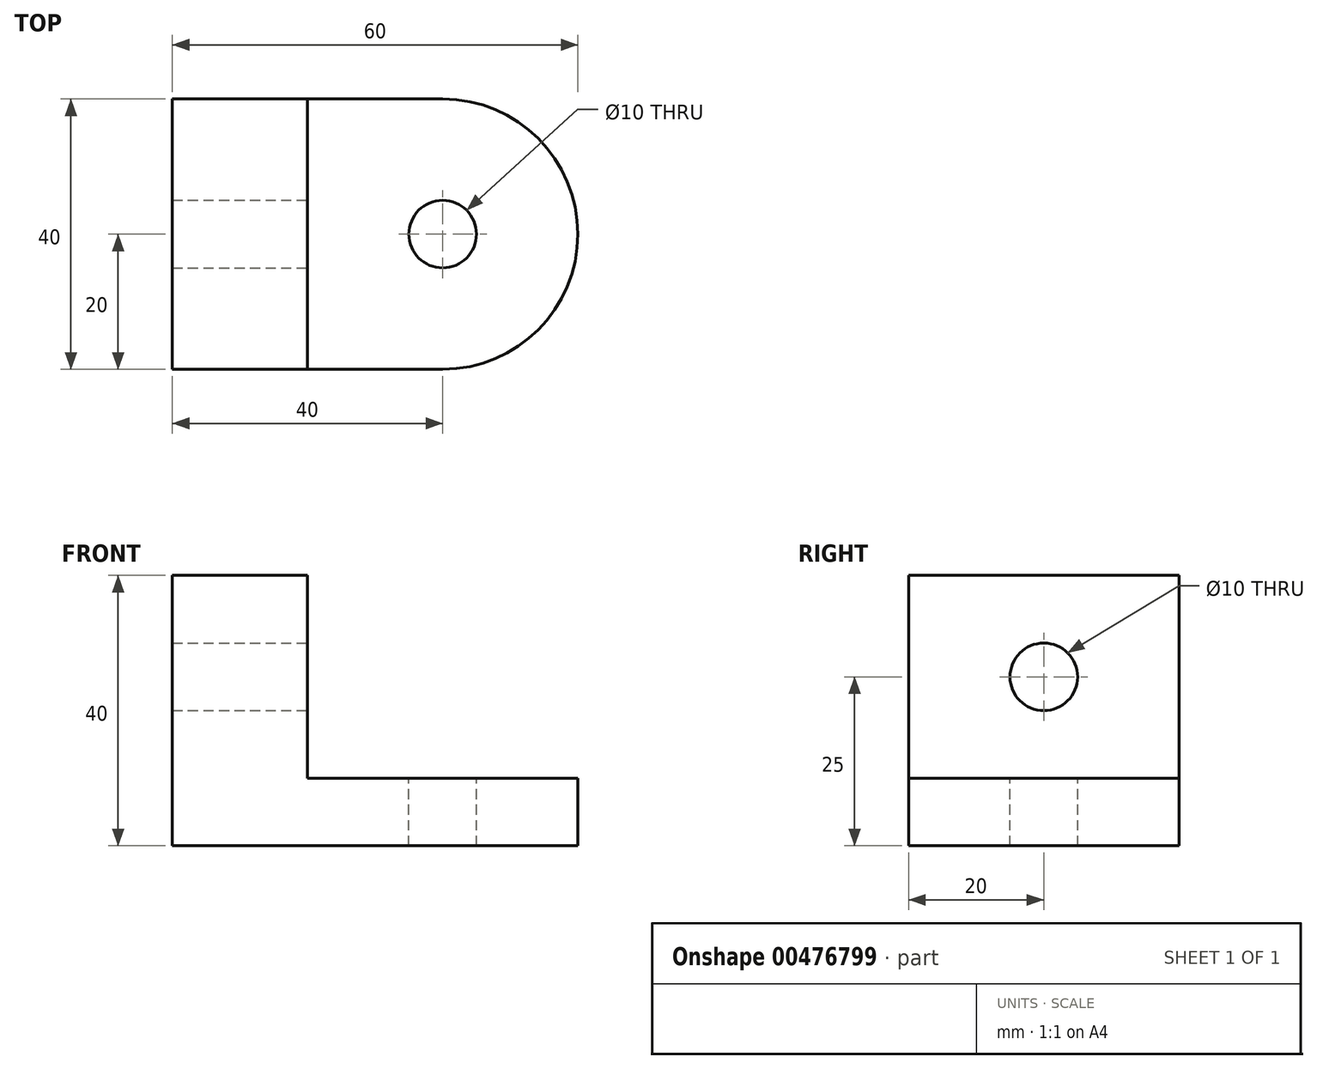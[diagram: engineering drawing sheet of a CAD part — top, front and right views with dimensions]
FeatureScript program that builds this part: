
annotation { "Feature Type Name" : "Feature", "Feature Type Description" : "" }
export const myFeature = defineFeature(function(context is Context, id is Id, definition is map)
    precondition{}
    {
        {
            var Q0;
            Q0=qCreatedBy(makeId("Front.planeOp"),FACE);
            var sketch = newSketch(context, id + "F0", { "sketchPlane" : qUnion([Q0])});
            skLineSegment(sketch, "E0", {"start": v(0, 0) * mm, "end": v(0, 20) * mm});
            skLineSegment(sketch, "E1", {"start": v(0, -20) * mm, "end": v(-20, -20) * mm});
            skLineSegment(sketch, "E2", {"start": v(-20, -20) * mm, "end": v(-20, 20) * mm});
            skLineSegment(sketch, "E3", {"start": v(-20, 20) * mm, "end": v(0, 20) * mm});
            skLineSegment(sketch, "E4", {"start": v(0, -20) * mm, "end": v(40, -20) * mm});
            skLineSegment(sketch, "E5", {"start": v(40, -20) * mm, "end": v(40, -10) * mm});
            skLineSegment(sketch, "E6", {"start": v(0, -10) * mm, "end": v(0, 0) * mm});
            skLineSegment(sketch, "E7", {"start": v(40, -10) * mm, "end": v(0, -10) * mm});
            skSolve(sketch);
        }
        {
            var Q0;
            Q0=makeQuery(id+"F0.imprint","IMPRINT",FACE,{"disambiguationData":[TD([[makeQuery(id+"F0.imprint","IMPRINT",EDGE,{"derivedFrom":sQuery(id+"F0.wireOp",EDGE,"E0")}),1.0]])]});
            extrude(context, id + "F1", {"entities" : qUnion([Q0]), "depth" : 40 * mm});
        }
        {
            var Q0;
            Q0=makeQuery(id+"F1.opExtrude","CAP_EDGE",EDGE,{"disambiguationData":[OSD([sQuery(id+"F0.wireOp",EDGE,"E5")])],"isStart":false});
            var Q1;
            Q1=makeQuery(id+"F1.opExtrude","CAP_EDGE",EDGE,{"disambiguationData":[OSD([sQuery(id+"F0.wireOp",EDGE,"E5")])],"isStart":true});
            fillet(context, id + "F2", {"entities" : qUnion([Q0, Q1]), "radius" : 20 * mm, "tangentPropagation" : true, "allowEdgeOverflow" : false});
        }
        {
            var Q0;
            Q0=makeQuery(id+"F1.opExtrude","SWEPT_FACE",FACE,{"disambiguationData":[OSD([sQuery(id+"F0.wireOp",EDGE,"E7")])]});
            var sketch = newSketch(context, id + "F3", { "sketchPlane" : qUnion([Q0])});
            skCircle(sketch, "E8", {"center": v(20, -20) * mm, "radius": 5 * mm});
            skSolve(sketch);
        }
        {
            var Q0;
            Q0 = qSketchRegion(id + "F3", true);
            extrude(context, id + "F4", {"entities" : qUnion([Q0]), "operationType" : NewBodyOperationType.REMOVE, "oppositeDirection" : true, "depth" : 25 * mm});
        }
        {
            var Q0;
            Q0=makeQuery(id+"F1.opExtrude","SWEPT_FACE",FACE,{"disambiguationData":[OSD([sQuery(id+"F0.wireOp",EDGE,"E0"),sQuery(id+"F0.wireOp",EDGE,"E6")])]});
            var sketch = newSketch(context, id + "F5", { "sketchPlane" : qUnion([Q0])});
            skCircle(sketch, "E9", {"center": v(-20, 5) * mm, "radius": 5 * mm});
            skSolve(sketch);
        }
        {
            var Q0;
            Q0=makeQuery(id+"F5.imprint","IMPRINT",FACE,{"disambiguationData":[TD([[makeQuery(id+"F5.imprint","IMPRINT",EDGE,{"derivedFrom":sQuery(id+"F5.wireOp",EDGE,"E9")}),1.0]])]});
            extrude(context, id + "F6", {"entities" : qUnion([Q0]), "operationType" : NewBodyOperationType.REMOVE, "oppositeDirection" : true, "depth" : 25 * mm});
        }
    });
